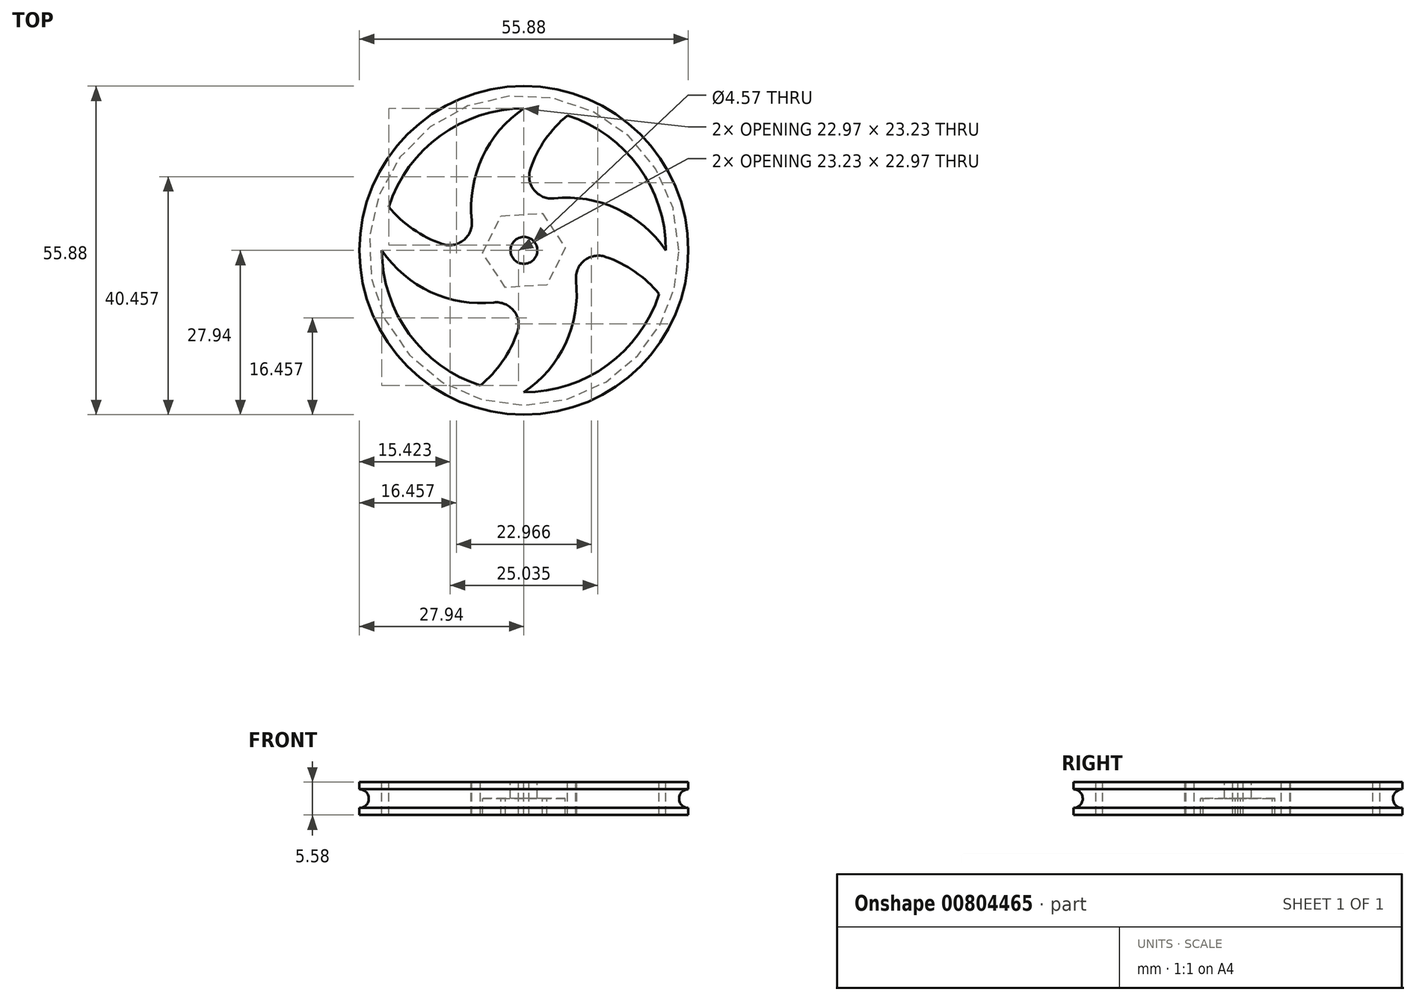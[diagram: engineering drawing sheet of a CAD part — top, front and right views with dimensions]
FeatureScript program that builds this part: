
annotation { "Feature Type Name" : "Feature", "Feature Type Description" : "" }
export const myFeature = defineFeature(function(context is Context, id is Id, definition is map)
    precondition{}
    {
        {
            var Q0;
            Q0=qCreatedBy(makeId("Top.planeOp"),FACE);
            var sketch = newSketch(context, id + "F0", { "sketchPlane" : qUnion([Q0])});
            skCircle(sketch, "E0", {"center": v(0, 0) * mm, "radius": 27.94 * mm});
            skCircle(sketch, "E1", {"center": v(0, 0) * mm, "radius": 24.13 * mm});
            skCircle(sketch, "E2", {"center": v(0, 0) * mm, "radius": 2.29 * mm});
            skCircle(sketch, "E3", {"center": v(0, 0) * mm, "radius": 7.62 * mm, "construction": true});
            skLineSegment(sketch, "E4", {"start": v(0, 24.13) * mm, "end": v(0, 7.62) * mm, "construction": true});
            skLineSegment(sketch, "E5", {"start": v(-24.13, 0) * mm, "end": v(-7.62, 0) * mm, "construction": true});
            skLineSegment(sketch, "E6", {"start": v(7.62, 0) * mm, "end": v(24.13, 0) * mm, "construction": true});
            skLineSegment(sketch, "E7", {"start": v(0, -7.62) * mm, "end": v(0, -24.13) * mm, "construction": true});
            skArc(sketch, "E8", {"start": v(0, 24.13) * mm, "mid": v(-8.02, 13.4) * mm, "end": v(-7.62, 0) * mm});
            skArc(sketch, "E9", {"start": v(7.4, 22.97) * mm, "mid": v(2.02, 16.1) * mm, "end": v(0, 7.62) * mm});
            skLineSegment(sketch, "E10", {"start": v(11.35, 7.28) * mm, "end": v(20.32, 7.28) * mm, "construction": true});
            skArc(sketch, "E11.1.0", {"start": v(-24.13, 0) * mm, "mid": v(-13.4, -8.02) * mm, "end": v(0, -7.62) * mm});
            skArc(sketch, "E11.1.1", {"start": v(-22.97, 7.4) * mm, "mid": v(-16.1, 2.02) * mm, "end": v(-7.62, 0) * mm});
            skArc(sketch, "E11.2.0", {"start": v(0, -24.13) * mm, "mid": v(8.02, -13.4) * mm, "end": v(7.62, 0) * mm});
            skArc(sketch, "E11.2.1", {"start": v(-7.4, -22.97) * mm, "mid": v(-2.02, -16.1) * mm, "end": v(0, -7.62) * mm});
            skArc(sketch, "E11.3.0", {"start": v(24.13, 0) * mm, "mid": v(13.4, 8.02) * mm, "end": v(0, 7.62) * mm});
            skArc(sketch, "E11.3.1", {"start": v(22.97, -7.4) * mm, "mid": v(16.1, -2.02) * mm, "end": v(7.62, 0) * mm});
            skCircle(sketch, "E12.cCircle", {"center": v(0, 0) * mm, "radius": 6.1 * mm, "construction": true});
            skLineSegment(sketch, "E12.0", {"start": v(7.02, 0.45) * mm, "end": v(3.9, -5.86) * mm});
            skLineSegment(sketch, "E12.1", {"start": v(3.9, -5.86) * mm, "end": v(-3.13, -6.3) * mm});
            skLineSegment(sketch, "E12.2", {"start": v(-3.13, -6.3) * mm, "end": v(-7.02, -0.45) * mm});
            skLineSegment(sketch, "E12.3", {"start": v(-7.02, -0.45) * mm, "end": v(-3.9, 5.86) * mm});
            skLineSegment(sketch, "E12.4", {"start": v(-3.9, 5.86) * mm, "end": v(3.13, 6.3) * mm});
            skLineSegment(sketch, "E12.5", {"start": v(3.13, 6.3) * mm, "end": v(7.02, 0.45) * mm});
            skPoint(sketch, "E12.0.midPoint", {"position": v(5.46, -2.7) * mm});
            skSolve(sketch);
        }
        {
            var Q0;
            Q0 = qSketchRegion(id + "F0", true);
            var Q1;
            Q1=makeQuery(id+"F0.imprint","IMPRINT",FACE,{"disambiguationData":[TD([[makeQuery(id+"F0.imprint","IMPRINT",EDGE,{"derivedFrom":sQuery(id+"F0.wireOp",EDGE,"E2")}),-1.0]])]});
            var Q2;
            {var subQ0=sQuery(id+"F0.wireOp",EDGE,"E8");Q2=makeQuery(id+"F0.imprint","IMPRINT",FACE,{"disambiguationData":[TD([[makeQuery(id+"F0.imprint","IMPRINT",EDGE,{"derivedFrom":subQ0}),1.0]])]});}
            var Q3;
            {var subQ0=sQuery(id+"F0.wireOp",EDGE,"d1HTXIdu-X3IE-UKNx-BBj5-efD1V8sTjuQk");Q3=makeQuery(id+"F0.imprint","IMPRINT",FACE,{"disambiguationData":[TD([[makeQuery(id+"F0.imprint","IMPRINT",EDGE,{"derivedFrom":subQ0}),1.0]])]});}
            var Q4;
            {var subQ0=sQuery(id+"F0.wireOp",EDGE,"E11.1.0");Q4=makeQuery(id+"F0.imprint","IMPRINT",FACE,{"disambiguationData":[TD([[makeQuery(id+"F0.imprint","IMPRINT",EDGE,{"derivedFrom":subQ0}),1.0]])]});}
            var Q5;
            {var subQ0=sQuery(id+"F0.wireOp",EDGE,"E11.2.0");Q5=makeQuery(id+"F0.imprint","IMPRINT",FACE,{"disambiguationData":[TD([[makeQuery(id+"F0.imprint","IMPRINT",EDGE,{"derivedFrom":subQ0}),1.0]])]});}
            var Q6;
            {var subQ0=sQuery(id+"F0.wireOp",EDGE,"E11.3.0");Q6=makeQuery(id+"F0.imprint","IMPRINT",FACE,{"disambiguationData":[TD([[makeQuery(id+"F0.imprint","IMPRINT",EDGE,{"derivedFrom":subQ0}),1.0]])]});}
            extrude(context, id + "F1", {"entities" : qUnion([Q0, Q1, Q2, Q3, Q4, Q5, Q6]), "endBound" : BoundingType.SYMMETRIC, "oppositeDirection" : true, "depth" : 5.6 * mm, "offsetDistance" : 25.4 * mm});
        }
        {
            var Q0;
            Q0=qCreatedBy(makeId("Front.planeOp"),FACE);
            var sketch = newSketch(context, id + "F2", { "sketchPlane" : qUnion([Q0])});
            skLineSegment(sketch, "E13", {"start": v(27.94, 0) * mm, "end": v(26.35, 0) * mm});
            skLineSegment(sketch, "E14", {"start": v(27.94, 1.59) * mm, "end": v(27.94, 0) * mm});
            skLineSegment(sketch, "E15.MirrorCS", {"start": v(27.94, -1.59) * mm, "end": v(27.94, 0) * mm});
            skLineSegment(sketch, "E16", {"start": v(0, 10) * mm, "end": v(0, -10.5) * mm, "construction": true});
            skArc(sketch, "E17", {"start": v(27.94, 1.59) * mm, "mid": v(26.35, 0) * mm, "end": v(27.94, -1.59) * mm});
            skSolve(sketch);
        }
        {
            var Q0;
            Q0=makeQuery(id+"F2.imprint","IMPRINT",FACE,{"disambiguationData":[TD([[makeQuery(id+"F2.imprint","IMPRINT",EDGE,{"derivedFrom":sQuery(id+"F2.wireOp",EDGE,"E13")}),1.0]])]});
            var Q1;
            Q1=makeQuery(id+"F2.imprint","IMPRINT",FACE,{"disambiguationData":[TD([[makeQuery(id+"F2.imprint","IMPRINT",EDGE,{"derivedFrom":sQuery(id+"F2.wireOp",EDGE,"E13")}),-1.0]])]});
            var Q2;
            Q2=sQuery(id+"F2.wireOp",EDGE,"E16");
            revolve(context, id + "F3", {"operationType" : NewBodyOperationType.REMOVE, "surfaceOperationType" : NewSurfaceOperationType.NEW, "entities" : qUnion([Q0, Q1]), "axis" : qUnion([Q2]), "revolveType" : RevolveType.FULL});
        }
        {
            var Q0;
            Q0=makeQuery(id+"F1.opExtrude","SWEPT_EDGE",EDGE,{"disambiguationData":[OSD([sQuery(id+"F0.wireOp",EDGE,"E3"),sQuery(id+"F0.wireOp",EDGE,"E8"),sQuery(id+"F0.wireOp",EDGE,"E11.1.1")])]});
            var Q1;
            Q1=makeQuery(id+"F1.opExtrude","SWEPT_EDGE",EDGE,{"disambiguationData":[OSD([sQuery(id+"F0.wireOp",EDGE,"E3"),sQuery(id+"F0.wireOp",EDGE,"E9"),sQuery(id+"F0.wireOp",EDGE,"E11.3.0")])]});
            var Q2;
            Q2=makeQuery(id+"F1.opExtrude","SWEPT_EDGE",EDGE,{"disambiguationData":[OSD([sQuery(id+"F0.wireOp",EDGE,"E3"),sQuery(id+"F0.wireOp",EDGE,"E11.2.0"),sQuery(id+"F0.wireOp",EDGE,"E11.3.1")])]});
            var Q3;
            Q3=makeQuery(id+"F1.opExtrude","SWEPT_EDGE",EDGE,{"disambiguationData":[OSD([sQuery(id+"F0.wireOp",EDGE,"E3"),sQuery(id+"F0.wireOp",EDGE,"E11.1.0"),sQuery(id+"F0.wireOp",EDGE,"E11.2.1")])]});
            fillet(context, id + "F4", {"entities" : qUnion([Q0, Q1, Q2, Q3]), "radius" : 3.8 * mm, "tangentPropagation" : true, "allowEdgeOverflow" : false});
        }
        {
            var Q0;
            Q0=makeQuery(id+"F0.imprint","IMPRINT",FACE,{"disambiguationData":[TD([[makeQuery(id+"F0.imprint","IMPRINT",EDGE,{"derivedFrom":sQuery(id+"F0.wireOp",EDGE,"E2")}),-1.0]])]});
            extrude(context, id + "F5", {"entities" : qUnion([Q0]), "operationType" : NewBodyOperationType.REMOVE, "oppositeDirection" : true, "depth" : 12.7 * mm, "offsetDistance" : 25.4 * mm});
        }
    });
